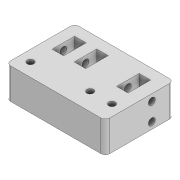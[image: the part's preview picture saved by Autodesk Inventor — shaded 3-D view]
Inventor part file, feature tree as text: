
AUTODESK INVENTOR PART (.ipt)
format: ipt  version: 2022 (Build 260153000, 153)  size: 184,832 bytes
history: native  units: mm
features: thicken_offset x3, extrude x2, fillet x1, sketch x1, projected_geometry x1
ambient origin geometry x8: Origin, YZ Plane, XZ Plane, XY Plane, X Axis, Y Axis, Z Axis, Center Point
bodies: Solid1 (feature_tree)
feature tree (8):
  extrude  "Extrusion1"  Depth=2.0mm
  fillet  "Fillet1"  Radius=25.0mm
  extrude  "Extrusion2"  Depth=2.0mm
  thicken_offset  "Thicken1"
  thicken_offset  "Thicken2"
  thicken_offset  "Thicken3"
  sketch  "Sketch2"  dims[d0=3.0mm d1=3.0mm d3=25.0mm d4=2.0mm d5=8.0mm d6=6.0mm d7=5.0mm d9=3.0mm d10=9.9mm d11=5.0mm d12=10.0mm d13=5.0mm d14=5.0mm d15=5.0mm d16=5.0mm d17=14.0mm d18=0.0mm d20=2.0mm d21=3.1mm d22=3.1mm d23=3.0mm d24=3.0mm d25=50.0mm d26=0.0mm d31=0.1mm d32=0.1mm d33=0.1mm d34=0.1mm d35=5.0mm d36=5.0mm d37=5.0mm d38=14.2mm d39=5.0mm d40=0.1mm d41=0.1mm]
  projected_geometry  "Projected Loop1"
